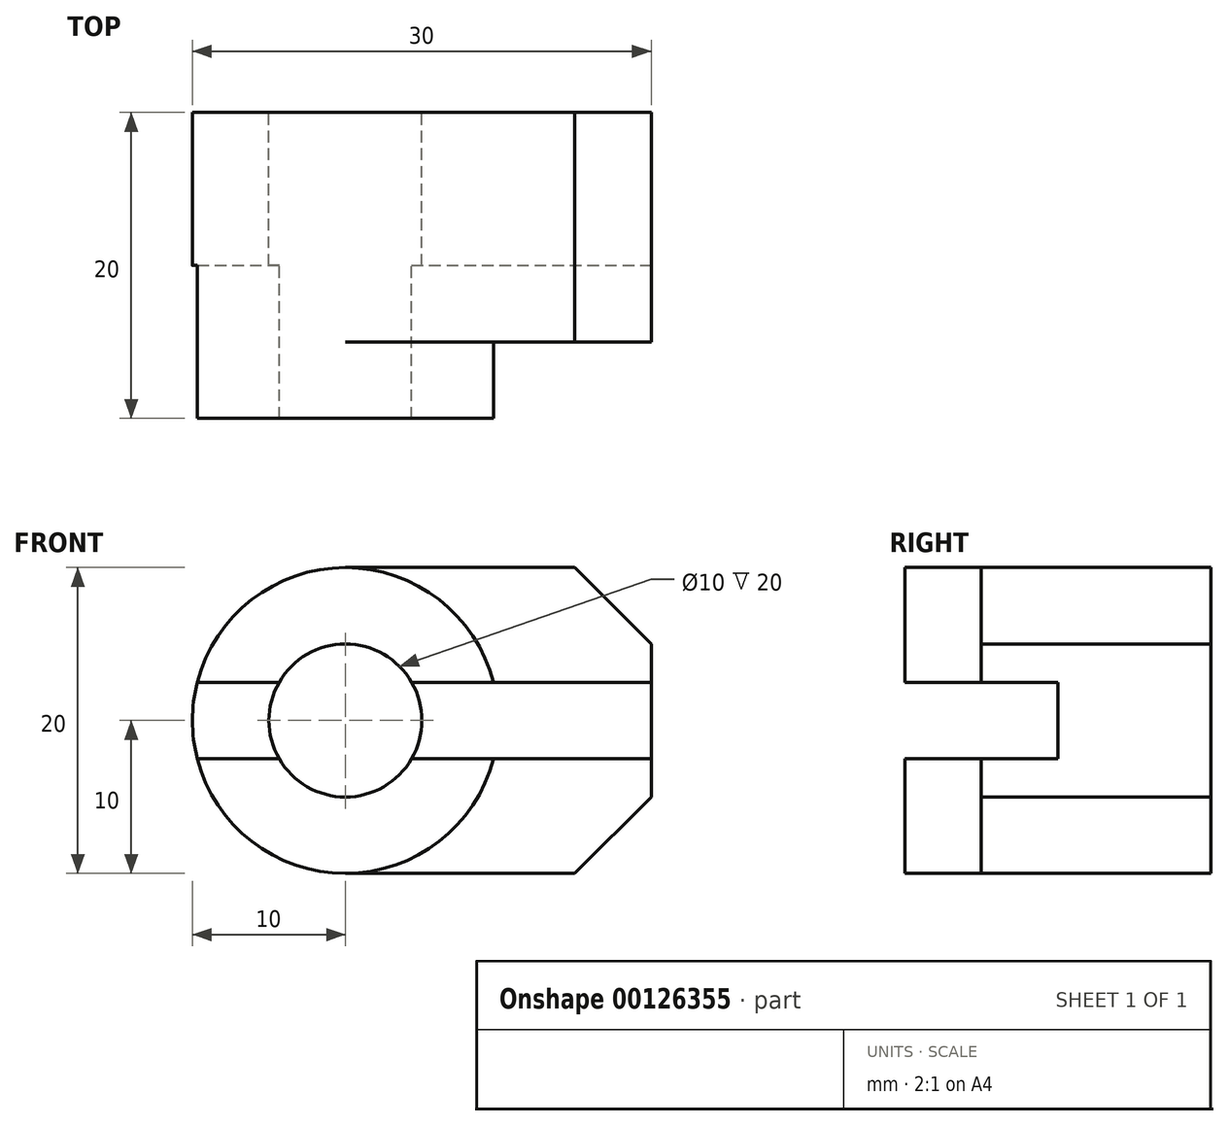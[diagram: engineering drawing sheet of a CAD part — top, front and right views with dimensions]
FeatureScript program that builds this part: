
annotation { "Feature Type Name" : "Feature", "Feature Type Description" : "" }
export const myFeature = defineFeature(function(context is Context, id is Id, definition is map)
    precondition{}
    {
        {
            var Q0;
            Q0=qCreatedBy(makeId("Front.planeOp"),FACE);
            var sketch = newSketch(context, id + "F0", { "sketchPlane" : qUnion([Q0])});
            skCircle(sketch, "E0", {"center": v(0, 0) * mm, "radius": 10 * mm});
            skLineSegment(sketch, "E1", {"start": v(0, 0) * mm, "end": v(0, 10) * mm, "construction": true});
            skLineSegment(sketch, "E2", {"start": v(0, 10) * mm, "end": v(0, -10) * mm, "construction": true});
            skLineSegment(sketch, "E3", {"start": v(0, 10) * mm, "end": v(15, 10) * mm});
            skLineSegment(sketch, "E4", {"start": v(0, -10) * mm, "end": v(15, -10) * mm});
            skLineSegment(sketch, "E5", {"start": v(0, 0) * mm, "end": v(20, 0) * mm, "construction": true});
            skLineSegment(sketch, "E6", {"start": v(20, 0) * mm, "end": v(20, 5) * mm});
            skLineSegment(sketch, "E7", {"start": v(20, 0) * mm, "end": v(20, -5) * mm});
            skLineSegment(sketch, "E8", {"start": v(20, -5) * mm, "end": v(15, -10) * mm});
            skLineSegment(sketch, "E9", {"start": v(15, 10) * mm, "end": v(20, 5) * mm});
            skSolve(sketch);
        }
        {
            var Q0;
            {var subQ0=sQuery(id+"F0.wireOp",EDGE,"E0");var subQ1=makeQuery(id+"F0.imprint","INTERSECT",VERTEX,{"derivedFrom":[subQ0,sQuery(id+"F0.wireOp",EDGE,"E3")]});Q0=makeQuery(id+"F0.imprint","IMPRINT",FACE,{"disambiguationData":[TD([[makeQuery(id+"F0.imprint","IMPRINT",EDGE,{"disambiguationData":[TD([[subQ1,-1.0]])],"derivedFrom":subQ0}),1.0]])]});}
            extrude(context, id + "F1", {"entities" : qUnion([Q0]), "depth" : 20 * mm});
        }
        {
            var Q0;
            {var subQ1=sQuery(id+"F0.wireOp",EDGE,"E3");Q0=makeQuery(id+"F0.imprint","IMPRINT",FACE,{"disambiguationData":[TD([[makeQuery(id+"F0.imprint","IMPRINT",EDGE,{"derivedFrom":subQ1}),-1.0]])]});}
            extrude(context, id + "F2", {"entities" : qUnion([Q0]), "operationType" : NewBodyOperationType.ADD, "depth" : 15 * mm});
        }
        {
            var Q0;
            Q0=makeQuery(id+"F2.opExtrude","SWEPT_FACE",FACE,{"disambiguationData":[OSD([sQuery(id+"F0.wireOp",EDGE,"E6"),sQuery(id+"F0.wireOp",EDGE,"E7")])]});
            var sketch = newSketch(context, id + "F3", { "sketchPlane" : qUnion([Q0])});
            skLineSegment(sketch, "E10", {"start": v(0, 0) * mm, "end": v(0, 2.5) * mm, "construction": true});
            skLineSegment(sketch, "E11", {"start": v(0, 2.5) * mm, "end": v(-10, 2.5) * mm, "construction": true});
            skLineSegment(sketch, "E12", {"start": v(-10, 2.5) * mm, "end": v(-10, -2.5) * mm});
            skLineSegment(sketch, "E13", {"start": v(-10, -2.5) * mm, "end": v(-20, -2.5) * mm});
            skLineSegment(sketch, "E14", {"start": v(-20, -2.5) * mm, "end": v(-20, 2.5) * mm});
            skLineSegment(sketch, "E15", {"start": v(-20, 2.5) * mm, "end": v(-10, 2.5) * mm});
            skSolve(sketch);
        }
        {
            var Q0;
            {var subQ0=sQuery(id+"F3.wireOp",EDGE,"E14");Q0=makeQuery(id+"F3.imprint","IMPRINT",FACE,{"disambiguationData":[TD([[makeQuery(id+"F3.imprint","IMPRINT",EDGE,{"derivedFrom":subQ0}),-1.0]])]});}
            var Q1;
            {var subQ0=sQuery(id+"F3.wireOp",EDGE,"E12");Q1=makeQuery(id+"F3.imprint","IMPRINT",FACE,{"disambiguationData":[TD([[makeQuery(id+"F3.imprint","IMPRINT",EDGE,{"derivedFrom":subQ0}),-1.0]])]});}
            extrude(context, id + "F4", {"entities" : qUnion([Q0, Q1]), "operationType" : NewBodyOperationType.REMOVE, "oppositeDirection" : true, "depth" : 30 * mm});
        }
        {
            var Q0;
            Q0=qCreatedBy(makeId("Front.planeOp"),FACE);
            var sketch = newSketch(context, id + "F5", { "sketchPlane" : qUnion([Q0])});
            skCircle(sketch, "E16", {"center": v(0, 0) * mm, "radius": 5 * mm});
            skSolve(sketch);
        }
        {
            var Q0;
            Q0=makeQuery(id+"F5.imprint","IMPRINT",FACE,{"disambiguationData":[TD([[makeQuery(id+"F5.imprint","IMPRINT",EDGE,{"derivedFrom":sQuery(id+"F5.wireOp",EDGE,"E16")}),1.0]])]});
            var Q1;
            Q1=sQuery(id+"F5.wireOp",EDGE,"E16");
            extrude(context, id + "F6", {"entities" : qUnion([Q0]), "operationType" : NewBodyOperationType.REMOVE, "surfaceEntities" : qUnion([Q1]), "depth" : 25 * mm});
        }
    });
